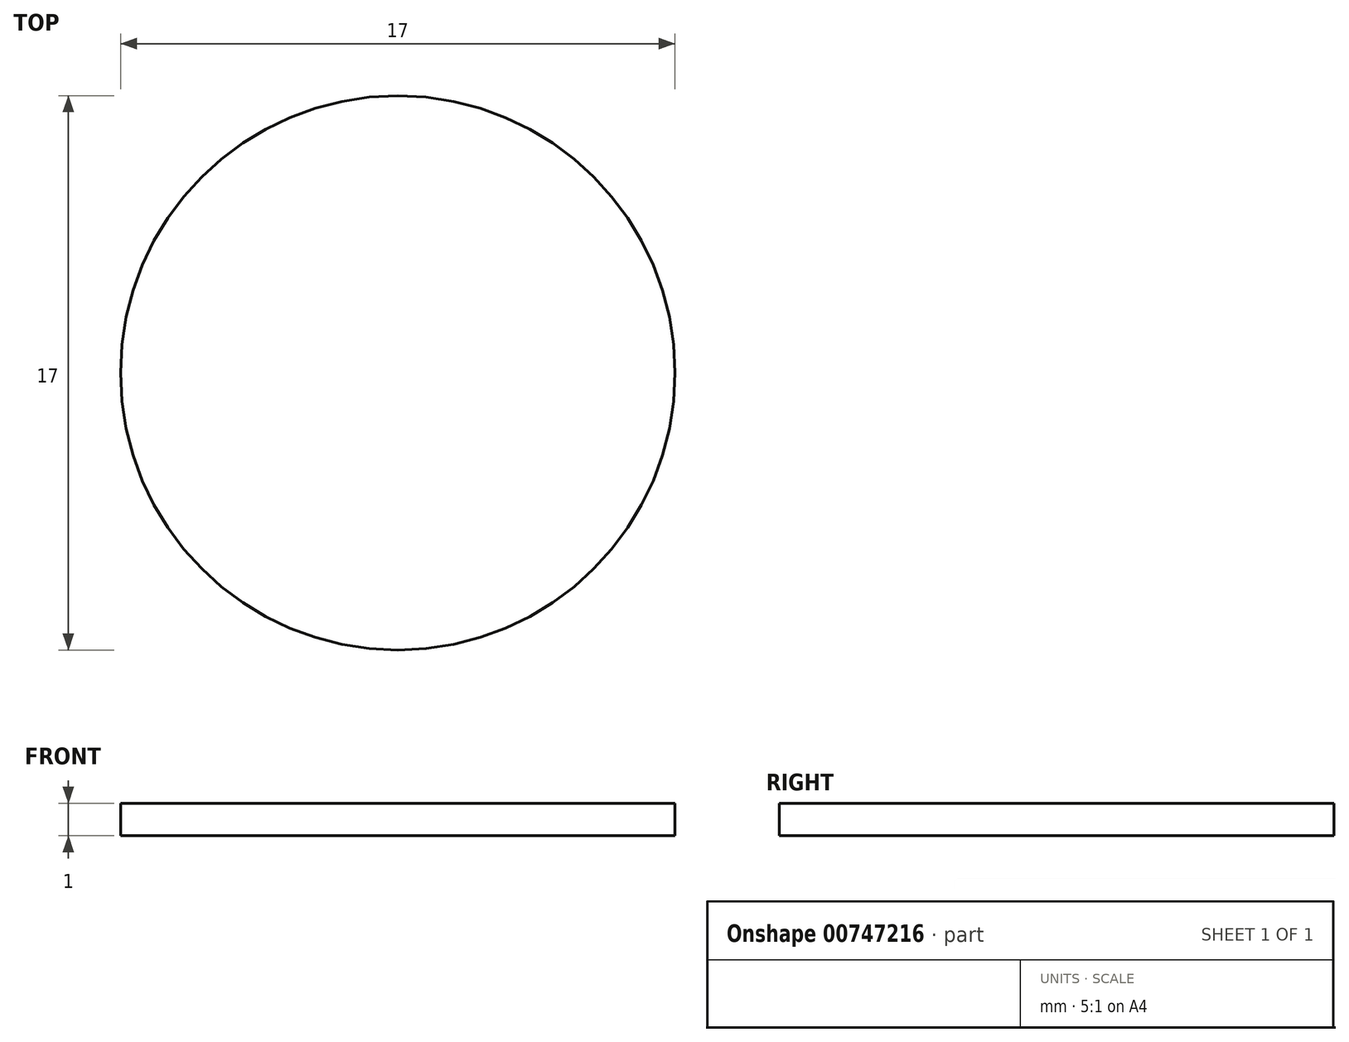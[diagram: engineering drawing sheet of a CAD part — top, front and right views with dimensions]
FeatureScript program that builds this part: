
annotation { "Feature Type Name" : "Feature", "Feature Type Description" : "" }
export const myFeature = defineFeature(function(context is Context, id is Id, definition is map)
    precondition{}
    {
        {
            var Q0;
            Q0=qCreatedBy(makeId("Top.planeOp"),FACE);
            var sketch = newSketch(context, id + "F0", { "sketchPlane" : qUnion([Q0])});
            skCircle(sketch, "E0", {"center": v(0, 0) * mm, "radius": 8.5 * mm});
            skSolve(sketch);
        }
        {
            var Q0;
            Q0=makeQuery(id+"F0.imprint","IMPRINT",FACE,{"disambiguationData":[TD([[makeQuery(id+"F0.imprint","IMPRINT",EDGE,{"derivedFrom":sQuery(id+"F0.wireOp",EDGE,"E0")}),1.0]])]});
            extrude(context, id + "F1", {"entities" : qUnion([Q0]), "depth" : 1 * mm, "offsetDistance" : 25 * mm});
        }
    });
